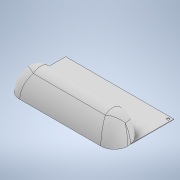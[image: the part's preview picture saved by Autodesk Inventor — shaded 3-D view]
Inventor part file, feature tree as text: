
AUTODESK INVENTOR PART (.ipt)
format: ipt  version: 2021 (Build 250183000, 183)  size: 187,392 bytes
history: native  units: mm
features: extrude x3, sketch x3, fillet x2
ambient origin geometry x8: Origin, YZ Plane, XZ Plane, XY Plane, X Axis, Y Axis, Z Axis, Center Point
bodies: Solid1 (feature_tree)
feature tree (8):
  extrude  "Extrusion1"  Depth=60.0mm
  extrude  "Extrusion4"  Depth=200.0mm
  fillet  "Fillet1"  Radius=50.0mm
  fillet  "Fillet2"  Radius=50.0mm
  extrude  "Extrusion6"  Depth=20.0mm
  sketch  "Sketch1"  dims[d0=200.0mm d1=60.0mm]
  sketch  "Sketch4"  dims[d2=1.0mm d3=0.0mm d12=200.0mm d13=50.0mm d14=50.0mm d15=0.0mm]
  sketch  "Sketch6"  dims[d16=50.0mm d17=20.0mm d24=5.0mm d25=5.0mm d26=5.0mm d27=5.0mm d28=1.0mm d29=0.0mm]
